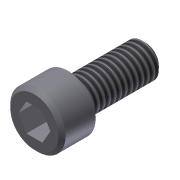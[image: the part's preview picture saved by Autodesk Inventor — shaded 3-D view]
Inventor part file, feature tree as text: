
AUTODESK INVENTOR PART (.ipt)
format: ipt  version: 2011 (Build 150239000, 239)  size: 108,032 bytes
history: native  units: in
note: dims shown in document units (in); Inventor stores cm internally (conversion verified against a paired STEP export)
features: extrude x3, sketch x3, chamfer x2, thread x1
ambient origin geometry x8: Origin, YZ Plane, XZ Plane, XY Plane, X Axis, Y Axis, Z Axis, Center Point
bodies: Solid1 (feature_tree)
feature tree (9):
  extrude  "Extrusion1"  Depth=0.19in TaperAngle=0.0deg
  extrude  "Extrusion2"  Depth=0.438in TaperAngle=0.0deg
  extrude  "Extrusion3"  Depth=0.125in TaperAngle=0.0deg
  thread  "Thread1"  [1 undecoded]
  chamfer  "Chamfer1"  Distance=0.02in Angle=45.0deg
  chamfer  "Chamfer2"  Distance=0.02in Angle=45.0deg
  sketch  "Sketch1"  dims[d0=0.312in d1=0.19in d2=0.0in]
  sketch  "Sketch2"  dims[d3=0.19in d4=0.438in d5=0.0in]
  sketch  "Sketch3"  dims[d6=0.1562in d7=0.125in d8=0.0in d9=1.0in d10=0.0in d11=0.02in d12=0.125in d13=45.0deg d14=0.02in d15=0.125in d16=45.0deg]
note: 1 required parameter value undecoded (feature->parameter linkage not recoverable at this tier; creation-order binding heuristic only, values carry confidence <= 0.55)
